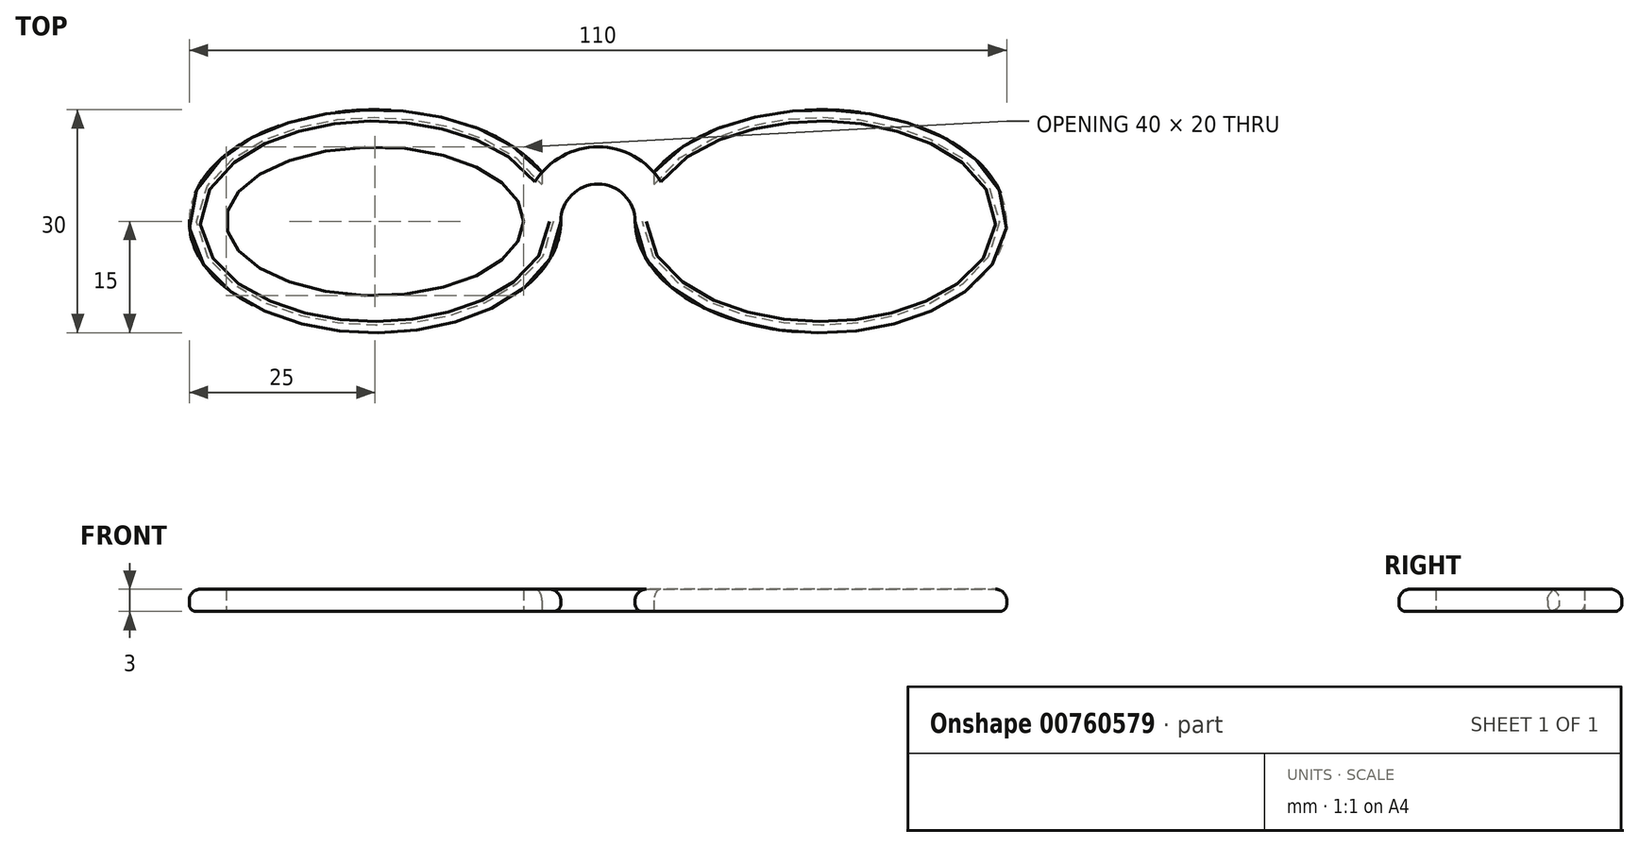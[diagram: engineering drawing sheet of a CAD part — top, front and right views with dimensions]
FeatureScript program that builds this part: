
annotation { "Feature Type Name" : "Feature", "Feature Type Description" : "" }
export const myFeature = defineFeature(function(context is Context, id is Id, definition is map)
    precondition{}
    {
        {
            var Q0;
            Q0=qCreatedBy(makeId("Top.planeOp"),FACE);
            var sketch = newSketch(context, id + "F0", { "sketchPlane" : qUnion([Q0])});
            skEllipticalArc(sketch, "E0", {});
            skFitSpline(sketch, "E1.0", {"points": [v(-19.96, 0.66) * mm, v(-20.02, 0) * mm, v(-19.96, -0.66) * mm, v(-19.8, -1.35) * mm, v(-19.49, -2.09) * mm, v(-19.02, -2.89) * mm, v(-18.35, -3.74) * mm, v(-17.19, -4.9) * mm, v(-15.23, -6.35) * mm, v(-12.65, -7.63) * mm, v(-10.27, -8.49) * mm, v(-7.74, -9.2) * mm, v(-5, -9.7) * mm, v(-2.17, -9.96) * mm, v(0, -10.02) * mm, v(2.17, -9.96) * mm, v(5, -9.7) * mm, v(7.74, -9.2) * mm, v(10.27, -8.49) * mm, v(12.65, -7.63) * mm, v(15.23, -6.35) * mm, v(17.19, -4.9) * mm, v(18.35, -3.74) * mm, v(19.02, -2.89) * mm, v(19.49, -2.09) * mm, v(19.8, -1.35) * mm, v(19.96, -0.66) * mm, v(20.02, 0) * mm, v(19.96, 0.66) * mm, v(19.8, 1.35) * mm, v(19.49, 2.09) * mm, v(19.02, 2.89) * mm, v(18.35, 3.74) * mm, v(17.19, 4.9) * mm, v(15.23, 6.35) * mm, v(12.65, 7.63) * mm, v(10.27, 8.49) * mm, v(7.74, 9.2) * mm, v(5, 9.7) * mm, v(2.17, 9.96) * mm, v(0, 10.02) * mm, v(-2.17, 9.96) * mm, v(-5, 9.7) * mm, v(-7.74, 9.2) * mm, v(-10.27, 8.49) * mm, v(-12.65, 7.63) * mm, v(-15.23, 6.35) * mm, v(-17.19, 4.9) * mm, v(-18.35, 3.74) * mm, v(-19.02, 2.89) * mm, v(-19.49, 2.09) * mm, v(-19.8, 1.35) * mm, v(-19.96, 0.66) * mm, v(-20.02, 0) * mm, v(-19.96, -0.66) * mm, v(-19.96, 0.66) * mm]});
            skArc(sketch, "E2", {"start": v(-25, 0) * mm, "mid": v(-26.46, 3.54) * mm, "end": v(-30, 5) * mm});
            skArc(sketch, "E3.0", {"start": v(-22.47, 6.58) * mm, "mid": v(-25.86, 9.1) * mm, "end": v(-30, 10) * mm});
            skArc(sketch, "E4", {"start": v(-35, 0) * mm, "mid": v(-33.54, 3.54) * mm, "end": v(-30, 5) * mm});
            skArc(sketch, "E5", {"start": v(-37.53, 6.58) * mm, "mid": v(-34.14, 9.1) * mm, "end": v(-30, 10) * mm});
            skEllipticalArc(sketch, "E6", {});
            skEllipse(sketch, "E7", {"center": v(-60, 0) * mm, "majorRadius": 20 * mm, "minorRadius": 10 * mm, "majorAxis": v(1, 0)});
            const initialGuessF0  = {"E0": [0, 0, -1, 0, 0.025, 0.015, 0, 5.82922806046417], "E6": [-0.06, 0, 1, 0, 0.025, 0.015, 0.4539572467154162, 0]};
            skSetInitialGuess(sketch, initialGuessF0);
            skSolve(sketch);
        }
        {
            var Q0;
            Q0=makeQuery(id+"F0.imprint","IMPRINT",FACE,{"disambiguationData":[TD([[makeQuery(id+"F0.imprint","IMPRINT",EDGE,{"derivedFrom":sQuery(id+"F0.wireOp",EDGE,"E0")}),1.0]])]});
            extrude(context, id + "F1", {"entities" : qUnion([Q0]), "depth" : 3 * mm, "offsetDistance" : 25 * mm});
        }
        {
            var Q0;
            Q0=makeQuery(id+"F1.opExtrude","CAP_EDGE",EDGE,{"disambiguationData":[OSD([sQuery(id+"F0.wireOp",EDGE,"E0")])],"isStart":true});
            var Q1;
            Q1=makeQuery(id+"F1.opExtrude","CAP_EDGE",EDGE,{"disambiguationData":[OSD([sQuery(id+"F0.wireOp",EDGE,"E3.0"),sQuery(id+"F0.wireOp",EDGE,"E5")])],"isStart":true});
            fillet(context, id + "F2", {"entities" : qUnion([Q0, Q1]), "radius" : 1 * mm, "tangentPropagation" : true, "allowEdgeOverflow" : false});
        }
        {
            var Q0;
            Q0=makeQuery(id+"F1.opExtrude","CAP_EDGE",EDGE,{"disambiguationData":[OSD([sQuery(id+"F0.wireOp",EDGE,"E6")])],"isStart":false});
            fillet(context, id + "F3", {"entities" : qUnion([Q0]), "radius" : 1.5 * mm, "tangentPropagation" : true, "allowEdgeOverflow" : false});
        }
    });
